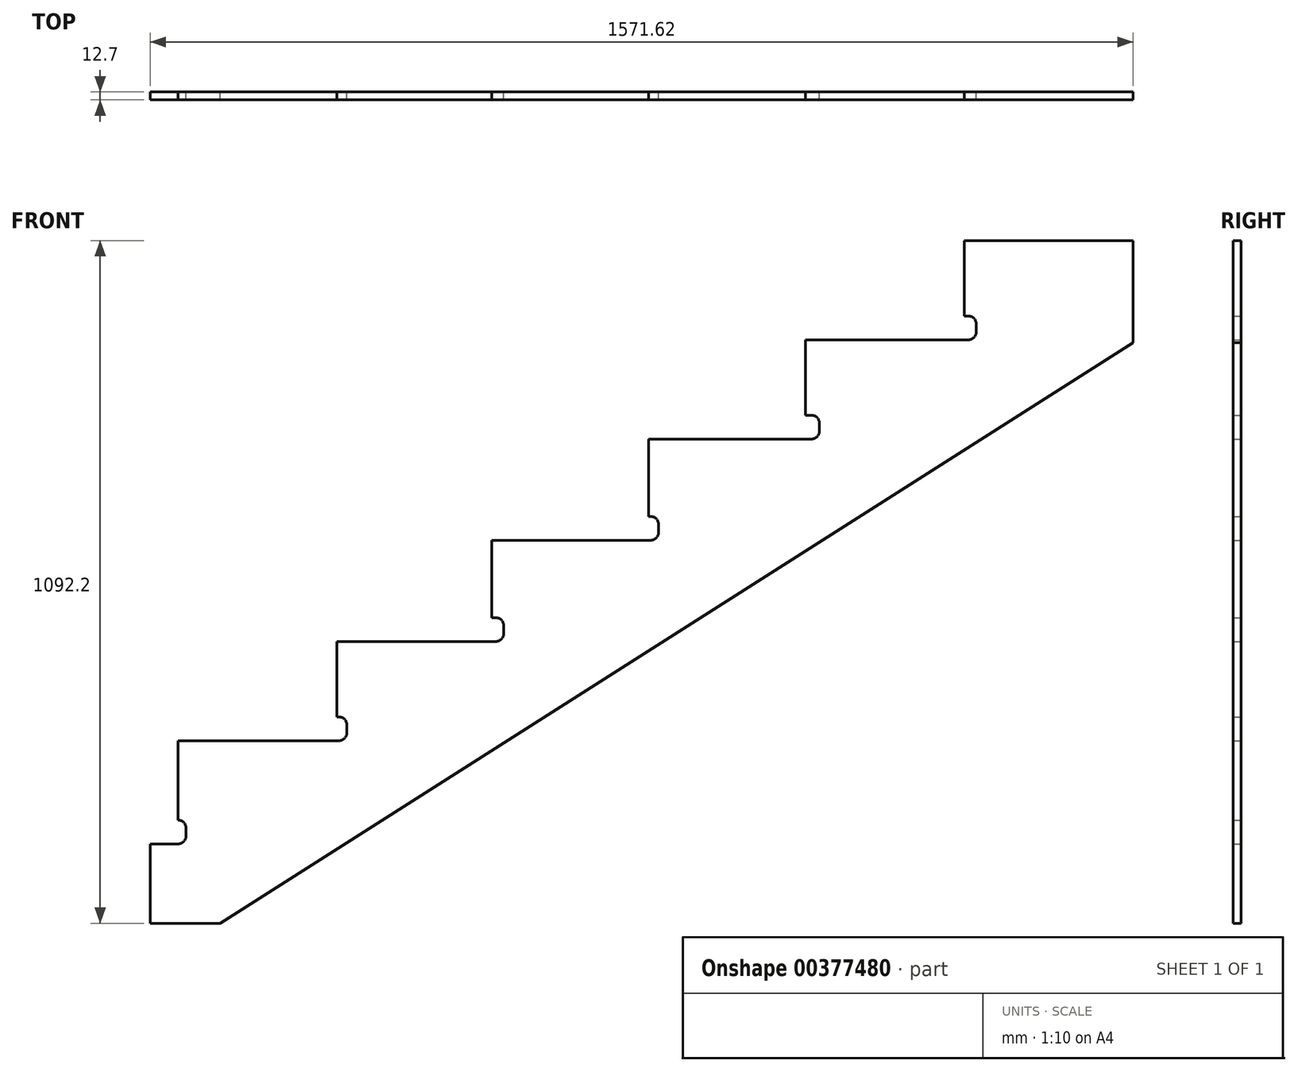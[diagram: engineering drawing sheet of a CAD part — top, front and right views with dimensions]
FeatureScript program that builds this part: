
annotation { "Feature Type Name" : "Feature", "Feature Type Description" : "" }
export const myFeature = defineFeature(function(context is Context, id is Id, definition is map)
    precondition{}
    {
        {
            var Q0;
            Q0=qCreatedBy(makeId("Front.planeOp"),FACE);
            var sketch = newSketch(context, id + "F0", { "sketchPlane" : qUnion([Q0])});
            skLineSegment(sketch, "E0", {"start": v(0, 0) * mm, "end": v(0, 127) * mm});
            skLineSegment(sketch, "E1", {"start": v(0, 127) * mm, "end": v(44.45, 127) * mm});
            skLineSegment(sketch, "E2", {"start": v(57.15, 139.7) * mm, "end": v(57.15, 152.4) * mm});
            skLineSegment(sketch, "E3", {"start": v(44.45, 165.1) * mm, "end": v(44.45, 165.1) * mm});
            skLineSegment(sketch, "E4", {"start": v(44.45, 165.1) * mm, "end": v(44.45, 292.1) * mm});
            skLineSegment(sketch, "E5", {"start": v(44.45, 292.1) * mm, "end": v(301.63, 292.1) * mm});
            skLineSegment(sketch, "E6", {"start": v(314.33, 304.8) * mm, "end": v(314.33, 317.5) * mm});
            skLineSegment(sketch, "E7", {"start": v(301.63, 330.2) * mm, "end": v(298.45, 330.2) * mm});
            skLineSegment(sketch, "E8", {"start": v(298.45, 330.2) * mm, "end": v(298.45, 450.85) * mm});
            skLineSegment(sketch, "E9", {"start": v(298.45, 450.85) * mm, "end": v(552.45, 450.85) * mm});
            skLineSegment(sketch, "E10", {"start": v(565.15, 463.55) * mm, "end": v(565.15, 476.25) * mm});
            skLineSegment(sketch, "E11", {"start": v(552.45, 488.95) * mm, "end": v(546.1, 488.95) * mm});
            skLineSegment(sketch, "E12", {"start": v(546.1, 488.95) * mm, "end": v(546.1, 612.78) * mm});
            skLineSegment(sketch, "E13", {"start": v(546.1, 612.78) * mm, "end": v(800.1, 612.78) * mm});
            skLineSegment(sketch, "E14", {"start": v(812.8, 625.48) * mm, "end": v(812.8, 638.18) * mm});
            skLineSegment(sketch, "E15", {"start": v(800.1, 650.88) * mm, "end": v(796.93, 650.88) * mm});
            skLineSegment(sketch, "E16", {"start": v(796.93, 650.88) * mm, "end": v(796.93, 774.7) * mm});
            skLineSegment(sketch, "E17", {"start": v(796.93, 774.7) * mm, "end": v(1057.28, 774.7) * mm});
            skLineSegment(sketch, "E18", {"start": v(1069.98, 787.4) * mm, "end": v(1069.98, 800.1) * mm});
            skLineSegment(sketch, "E19", {"start": v(1057.28, 812.8) * mm, "end": v(1047.75, 812.8) * mm});
            skLineSegment(sketch, "E20", {"start": v(1047.75, 812.8) * mm, "end": v(1047.75, 933.45) * mm});
            skLineSegment(sketch, "E21", {"start": v(1047.75, 933.45) * mm, "end": v(1308.1, 933.45) * mm});
            skLineSegment(sketch, "E22", {"start": v(1320.8, 946.15) * mm, "end": v(1320.8, 958.85) * mm});
            skLineSegment(sketch, "E23", {"start": v(1308.1, 971.55) * mm, "end": v(1301.75, 971.55) * mm});
            skLineSegment(sketch, "E24", {"start": v(1301.75, 971.55) * mm, "end": v(1301.75, 1092.2) * mm});
            skLineSegment(sketch, "E25", {"start": v(1301.75, 1092.2) * mm, "end": v(1571.63, 1092.2) * mm});
            skLineSegment(sketch, "E26", {"start": v(1571.63, 1092.2) * mm, "end": v(1571.63, 928.99) * mm});
            skLineSegment(sketch, "E27", {"start": v(1571.63, 928.99) * mm, "end": v(111.78, 0) * mm});
            skLineSegment(sketch, "E28", {"start": v(111.78, 0) * mm, "end": v(0, 0) * mm});
            skLineSegment(sketch, "E29", {"start": v(44.45, 292.1) * mm, "end": v(1301.75, 1092.2) * mm, "construction": true});
            skPoint(sketch, "E30.visualSharp", {"position": v(57.15, 165.1) * mm});
            skArc(sketch, "E30.filletArc", {"start": v(57.15, 152.4) * mm, "mid": v(53.43, 161.38) * mm, "end": v(44.45, 165.1) * mm});
            skPoint(sketch, "E31.visualSharp", {"position": v(57.15, 127) * mm});
            skArc(sketch, "E31.filletArc", {"start": v(44.45, 127) * mm, "mid": v(53.43, 130.72) * mm, "end": v(57.15, 139.7) * mm});
            skPoint(sketch, "E32.visualSharp", {"position": v(314.33, 292.1) * mm});
            skArc(sketch, "E32.filletArc", {"start": v(301.63, 292.1) * mm, "mid": v(310.6, 295.82) * mm, "end": v(314.33, 304.8) * mm});
            skPoint(sketch, "E33.visualSharp", {"position": v(314.33, 330.2) * mm});
            skArc(sketch, "E33.filletArc", {"start": v(314.33, 317.5) * mm, "mid": v(310.6, 326.48) * mm, "end": v(301.63, 330.2) * mm});
            skPoint(sketch, "E34.visualSharp", {"position": v(565.15, 450.85) * mm});
            skArc(sketch, "E34.filletArc", {"start": v(552.45, 450.85) * mm, "mid": v(561.43, 454.57) * mm, "end": v(565.15, 463.55) * mm});
            skPoint(sketch, "E35.visualSharp", {"position": v(565.15, 488.95) * mm});
            skArc(sketch, "E35.filletArc", {"start": v(565.15, 476.25) * mm, "mid": v(561.43, 485.23) * mm, "end": v(552.45, 488.95) * mm});
            skPoint(sketch, "E36.visualSharp", {"position": v(812.8, 650.88) * mm});
            skArc(sketch, "E36.filletArc", {"start": v(812.8, 638.18) * mm, "mid": v(809.08, 647.16) * mm, "end": v(800.1, 650.88) * mm});
            skPoint(sketch, "E37.visualSharp", {"position": v(812.8, 612.78) * mm});
            skArc(sketch, "E37.filletArc", {"start": v(800.1, 612.78) * mm, "mid": v(809.08, 616.5) * mm, "end": v(812.8, 625.48) * mm});
            skPoint(sketch, "E38.visualSharp", {"position": v(1069.98, 774.7) * mm});
            skArc(sketch, "E38.filletArc", {"start": v(1057.28, 774.7) * mm, "mid": v(1066.26, 778.42) * mm, "end": v(1069.98, 787.4) * mm});
            skPoint(sketch, "E39.visualSharp", {"position": v(1069.98, 812.8) * mm});
            skArc(sketch, "E39.filletArc", {"start": v(1069.98, 800.1) * mm, "mid": v(1066.26, 809.08) * mm, "end": v(1057.28, 812.8) * mm});
            skPoint(sketch, "E40.visualSharp", {"position": v(1320.8, 933.45) * mm});
            skArc(sketch, "E40.filletArc", {"start": v(1308.1, 933.45) * mm, "mid": v(1317.08, 937.17) * mm, "end": v(1320.8, 946.15) * mm});
            skPoint(sketch, "E41.visualSharp", {"position": v(1320.8, 971.55) * mm});
            skArc(sketch, "E41.filletArc", {"start": v(1320.8, 958.85) * mm, "mid": v(1317.08, 967.83) * mm, "end": v(1308.1, 971.55) * mm});
            skLineSegment(sketch, "E42", {"start": v(111.78, 0) * mm, "end": v(111.78, 93.01) * mm, "construction": true});
            skLineSegment(sketch, "E43", {"start": v(0, 0) * mm, "end": v(1571.63, 1092.2) * mm, "construction": true});
            skSolve(sketch);
        }
        {
            var Q0;
            Q0 = qSketchRegion(id + "F0", true);
            extrude(context, id + "F1", {"entities" : qUnion([Q0]), "depth" : 12.7 * mm});
        }
    });
